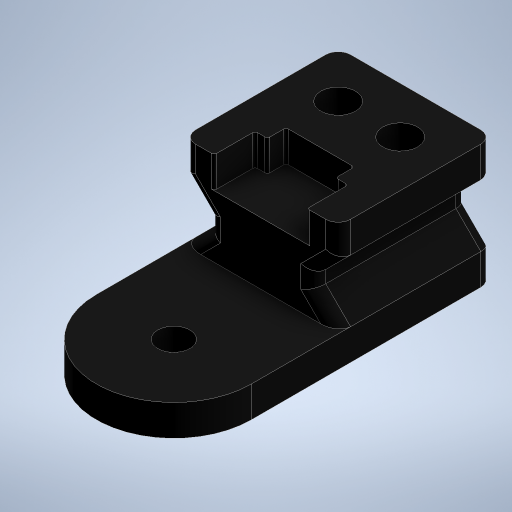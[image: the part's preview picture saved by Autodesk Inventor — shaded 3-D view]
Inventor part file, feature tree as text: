
AUTODESK INVENTOR PART (.ipt)
format: ipt  version: 2024.2 (Build 282272000, 272)  size: 326,656 bytes
history: native  units: mm
features: extrude x4, fillet x2, other x1, sketch x1, chamfer x1
ambient origin geometry x8: Origin, YZ Plane, XZ Plane, XY Plane, X Axis, Y Axis, Z Axis, Center Point
bodies: Body1 (feature_tree)
feature tree (9):
  other  "Bryła1"
  sketch  "Szkic1"
  extrude  "Wyciągnięcie proste1"  Depth=5.2mm
  extrude  "Wyciągnięcie proste2"  Depth=12.5mm
  extrude  "Wyciągnięcie proste3"  Depth=5.6mm
  extrude  "Wyciągnięcie proste4"  Depth=10.0mm
  chamfer  "Faza1"  Distance=4.0mm
  fillet  "Zaokrąglenie1"  Radius=14.0mm
  fillet  "Zaokrąglenie2"  Radius=25.0mm
